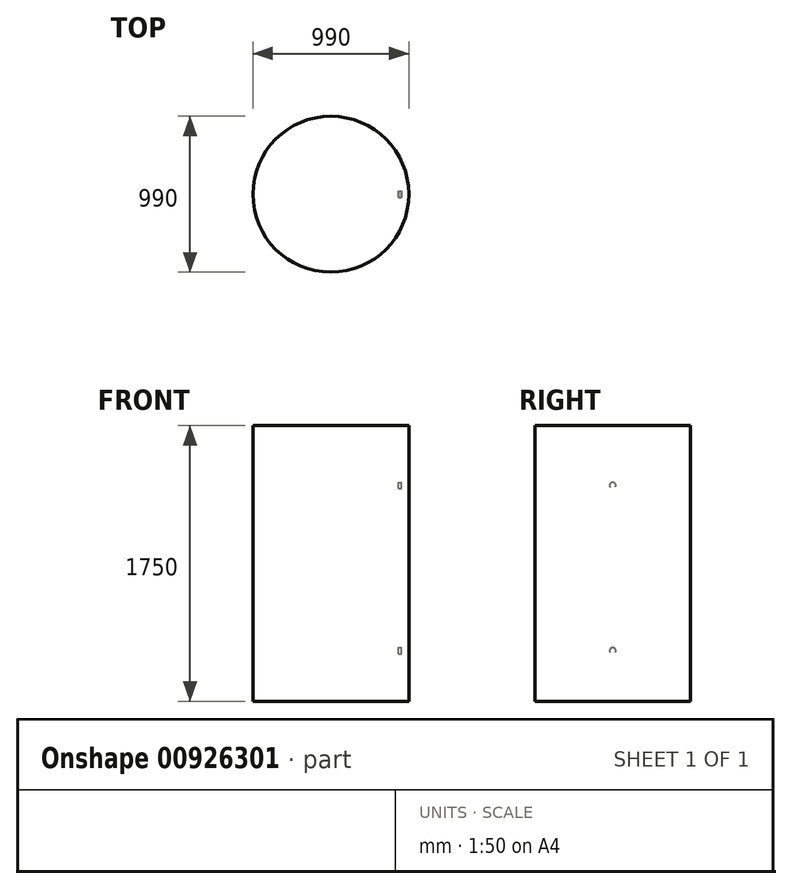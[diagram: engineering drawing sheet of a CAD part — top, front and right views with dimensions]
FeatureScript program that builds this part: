
annotation { "Feature Type Name" : "Feature", "Feature Type Description" : "" }
export const myFeature = defineFeature(function(context is Context, id is Id, definition is map)
    precondition{}
    {
        {
            var Q0;
            Q0=qCreatedBy(makeId("Top.planeOp"),FACE);
            var sketch = newSketch(context, id + "F0", { "sketchPlane" : qUnion([Q0])});
            skCircle(sketch, "E0", {"center": v(0, 0) * mm, "radius": 395 * mm});
            skCircle(sketch, "E1", {"center": v(0, 0) * mm, "radius": 495 * mm});
            skSolve(sketch);
        }
        {
            var Q0;
            Q0=makeQuery(id+"F0.imprint","IMPRINT",FACE,{"disambiguationData":[TD([[makeQuery(id+"F0.imprint","IMPRINT",EDGE,{"derivedFrom":sQuery(id+"F0.wireOp",EDGE,"E0")}),-1.0]])]});
            var Q1;
            Q1=makeQuery(id+"F0.imprint","IMPRINT",FACE,{"disambiguationData":[TD([[makeQuery(id+"F0.imprint","IMPRINT",EDGE,{"derivedFrom":sQuery(id+"F0.wireOp",EDGE,"E0")}),1.0]])]});
            var Q2;
            Q2=sQuery(id+"F0.wireOp",EDGE,"E1");
            extrude(context, id + "F1", {"entities" : qUnion([Q0, Q1]), "surfaceEntities" : qUnion([Q2]), "depth" : 1750 * mm, "offsetDistance" : 25 * mm});
        }
        {
            var Q0;
            Q0=qCreatedBy(makeId("Right.planeOp"),FACE);
            cPlane(context, id + "F2", {"entities" : qUnion([Q0]), "cplaneType" : CPlaneType.OFFSET, "offset" : 450 * mm, "width" : 150 * mm, "height" : 150 * mm});
        }
        {
            var Q0;
            Q0=qCreatedBy(id+"F2.planeOp",FACE);
            var sketch = newSketch(context, id + "F3", { "sketchPlane" : qUnion([Q0])});
            skCircle(sketch, "E2", {"center": v(0, 320) * mm, "radius": 20 * mm});
            skCircle(sketch, "E3", {"center": v(0, 1370) * mm, "radius": 20 * mm});
            skSolve(sketch);
        }
        {
            var Q0;
            Q0 = qSketchRegion(id + "F3", true);
            extrude(context, id + "F4", {"entities" : qUnion([Q0]), "oppositeDirection" : true, "depth" : 20 * mm, "offsetDistance" : 25 * mm});
        }
    });
